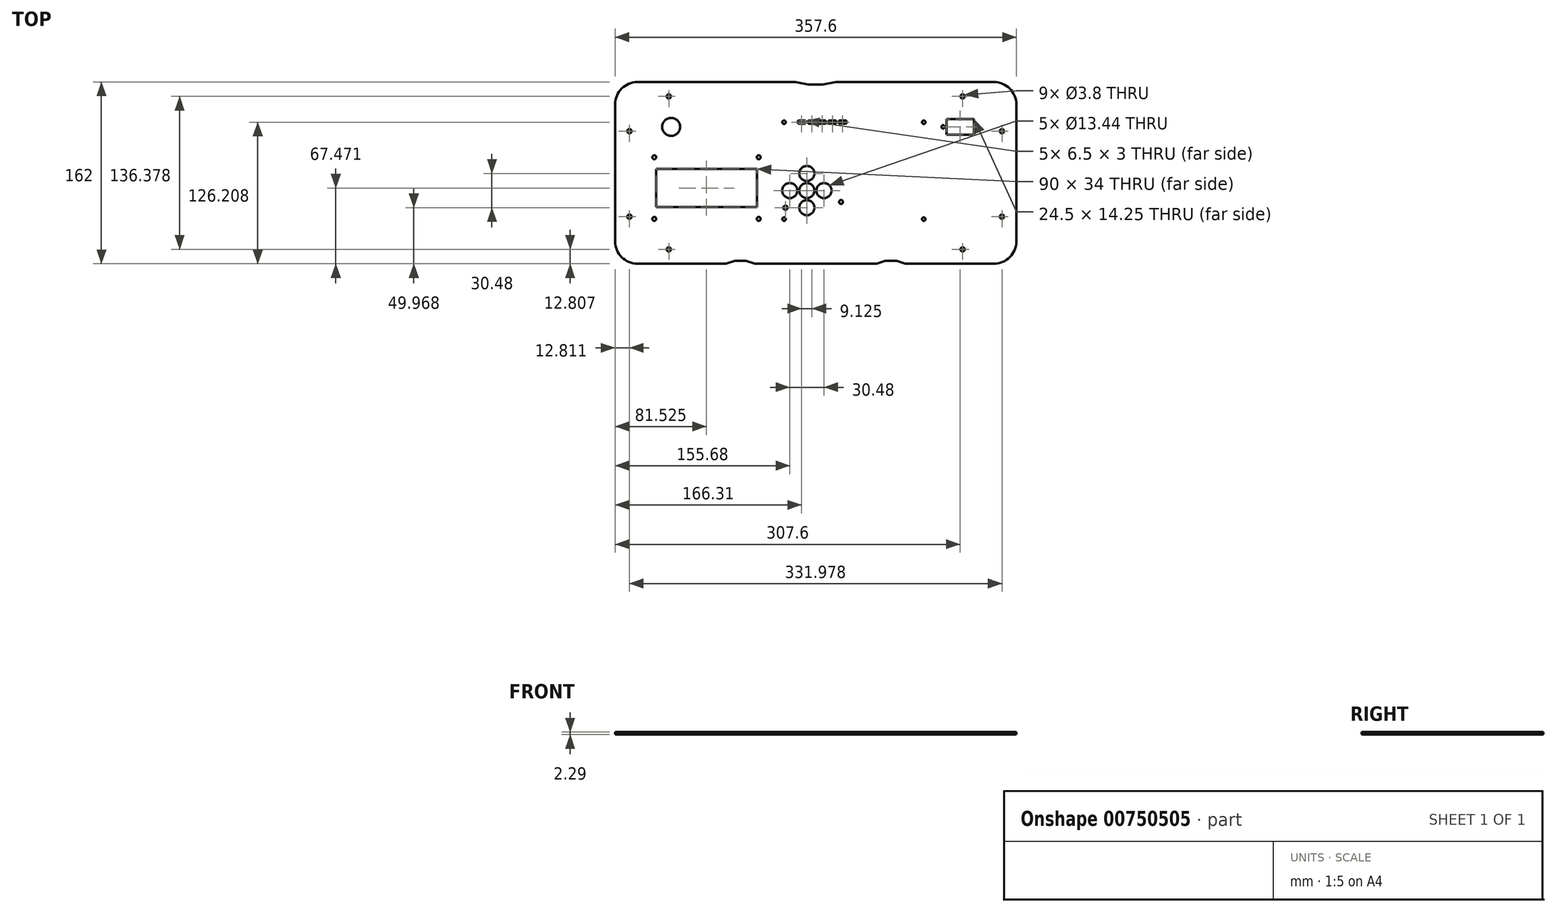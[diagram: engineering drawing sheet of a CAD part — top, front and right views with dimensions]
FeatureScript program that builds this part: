
annotation { "Feature Type Name" : "Feature", "Feature Type Description" : "" }
export const myFeature = defineFeature(function(context is Context, id is Id, definition is map)
    precondition{}
    {
        {
            var Q0;
            Q0=qCreatedBy(makeId("Top.planeOp"),FACE);
            var sketch = newSketch(context, id + "F0", { "sketchPlane" : qUnion([Q0])});
            skLineSegment(sketch, "E0.bottom", {"start": v(-158.73, 79.95) * mm, "end": v(-17.96, 79.95) * mm});
            skLineSegment(sketch, "E0.top", {"start": v(-158.73, -82.05) * mm, "end": v(-79.8, -82.05) * mm});
            skLineSegment(sketch, "E0.left", {"start": v(-178.8, 59.88) * mm, "end": v(-178.8, -61.99) * mm});
            skLineSegment(sketch, "E0.right", {"start": v(178.8, 59.88) * mm, "end": v(178.8, -61.99) * mm});
            skPoint(sketch, "E1.visualSharp", {"position": v(-178.8, 79.95) * mm});
            skArc(sketch, "E1.filletArc", {"start": v(-158.73, 79.95) * mm, "mid": v(-172.92, 74.07) * mm, "end": v(-178.8, 59.88) * mm});
            skPoint(sketch, "E2.visualSharp", {"position": v(-178.8, -82.05) * mm});
            skArc(sketch, "E2.filletArc", {"start": v(-178.8, -61.99) * mm, "mid": v(-172.92, -76.18) * mm, "end": v(-158.73, -82.05) * mm});
            skPoint(sketch, "E3.visualSharp", {"position": v(178.8, -82.05) * mm});
            skArc(sketch, "E3.filletArc", {"start": v(158.73, -82.05) * mm, "mid": v(172.92, -76.18) * mm, "end": v(178.8, -61.99) * mm});
            skPoint(sketch, "E4.visualSharp", {"position": v(178.8, 79.95) * mm});
            skArc(sketch, "E4.filletArc", {"start": v(178.8, 59.88) * mm, "mid": v(172.92, 74.07) * mm, "end": v(158.73, 79.95) * mm});
            skCircle(sketch, "E5", {"center": v(-130.9, 67.13) * mm, "radius": 1.9 * mm});
            skCircle(sketch, "E6", {"center": v(-165.99, 36.1) * mm, "radius": 1.9 * mm});
            skCircle(sketch, "E7", {"center": v(-165.99, -40.1) * mm, "radius": 1.9 * mm});
            skCircle(sketch, "E8", {"center": v(-130.9, -69.24) * mm, "radius": 1.9 * mm});
            skCircle(sketch, "E9.MirrorC", {"center": v(165.99, 36.1) * mm, "radius": 1.9 * mm});
            skCircle(sketch, "E10.MirrorC", {"center": v(130.9, 67.13) * mm, "radius": 1.9 * mm});
            skCircle(sketch, "E11.MirrorC", {"center": v(165.99, -40.1) * mm, "radius": 1.9 * mm});
            skCircle(sketch, "E12.MirrorC", {"center": v(130.9, -69.24) * mm, "radius": 1.9 * mm});
            skArc(sketch, "E13.0", {"start": v(-158.73, 60.9) * mm, "mid": v(-159.45, 60.6) * mm, "end": v(-159.75, 59.88) * mm});
            skLineSegment(sketch, "E13.1", {"start": v(-159.75, 59.88) * mm, "end": v(-159.75, -61.99) * mm, "construction": true});
            skLineSegment(sketch, "E13.2", {"start": v(-158.73, 60.9) * mm, "end": v(158.73, 60.9) * mm, "construction": true});
            skArc(sketch, "E13.3", {"start": v(-159.75, -61.99) * mm, "mid": v(-159.45, -62.7) * mm, "end": v(-158.73, -63) * mm});
            skArc(sketch, "E13.4", {"start": v(159.75, 59.88) * mm, "mid": v(159.45, 60.6) * mm, "end": v(158.73, 60.9) * mm});
            skLineSegment(sketch, "E13.5", {"start": v(159.75, 59.88) * mm, "end": v(159.75, -61.99) * mm, "construction": true});
            skArc(sketch, "E13.6", {"start": v(158.73, -63) * mm, "mid": v(159.45, -62.7) * mm, "end": v(159.75, -61.99) * mm});
            skLineSegment(sketch, "E13.7", {"start": v(-158.73, -63) * mm, "end": v(158.73, -63) * mm, "construction": true});
            skLineSegment(sketch, "E14", {"start": v(0, 79.95) * mm, "end": v(0, 0) * mm, "construction": true});
            skLineSegment(sketch, "E15", {"start": v(178.8, 0) * mm, "end": v(0, 0) * mm, "construction": true});
            skCircle(sketch, "E16", {"center": v(-128.8, 39.95) * mm, "radius": 8.05 * mm});
            skCircle(sketch, "E17", {"center": v(113.53, 39.95) * mm, "radius": 1.48 * mm});
            skLineSegment(sketch, "E18.bottom", {"start": v(116.55, 47.07) * mm, "end": v(141.05, 47.07) * mm});
            skLineSegment(sketch, "E18.top", {"start": v(116.55, 32.82) * mm, "end": v(141.05, 32.82) * mm});
            skLineSegment(sketch, "E18.left", {"start": v(116.55, 47.07) * mm, "end": v(116.55, 32.82) * mm});
            skLineSegment(sketch, "E18.right", {"start": v(141.05, 47.07) * mm, "end": v(141.05, 32.82) * mm});
            skLineSegment(sketch, "E19", {"start": v(141.05, 39.95) * mm, "end": v(116.55, 39.95) * mm, "construction": true});
            skCircle(sketch, "E20", {"center": v(144.08, 39.96) * mm, "radius": 1.48 * mm});
            skLineSegment(sketch, "E21", {"start": v(128.8, 47.07) * mm, "end": v(128.8, 32.82) * mm, "construction": true});
            skLineSegment(sketch, "E22", {"start": v(-6.5, 77.6) * mm, "end": v(6.5, 77.6) * mm});
            skLineSegment(sketch, "E23", {"start": v(0, 77.6) * mm, "end": v(0, 79.95) * mm, "construction": true});
            skLineSegment(sketch, "E24", {"start": v(6.5, 77.6) * mm, "end": v(17.96, 79.95) * mm});
            skLineSegment(sketch, "E25", {"start": v(-6.5, 77.6) * mm, "end": v(-17.96, 79.95) * mm});
            skLineSegment(sketch, "E26", {"start": v(17.96, 79.95) * mm, "end": v(158.73, 79.95) * mm});
            skPoint(sketch, "E27", {"position": v(-79.8, -82.05) * mm});
            skPoint(sketch, "E28", {"position": v(-54.3, -82.05) * mm});
            skLineSegment(sketch, "E29", {"start": v(-72.08, -79.45) * mm, "end": v(-62.08, -79.45) * mm});
            skLineSegment(sketch, "E30", {"start": v(-79.8, -82.05) * mm, "end": v(-72.08, -79.45) * mm});
            skLineSegment(sketch, "E31", {"start": v(-62.08, -79.45) * mm, "end": v(-54.3, -82.05) * mm});
            skLineSegment(sketch, "E32.trimOffspring", {"start": v(-54.3, -82.05) * mm, "end": v(54.3, -82.05) * mm});
            skPoint(sketch, "E33", {"position": v(79.8, -82.05) * mm});
            skPoint(sketch, "E34", {"position": v(54.3, -82.05) * mm});
            skLineSegment(sketch, "E35", {"start": v(62.08, -79.45) * mm, "end": v(72.08, -79.45) * mm});
            skLineSegment(sketch, "E36", {"start": v(79.8, -82.05) * mm, "end": v(72.08, -79.45) * mm});
            skLineSegment(sketch, "E37", {"start": v(54.3, -82.05) * mm, "end": v(62.08, -79.45) * mm});
            skLineSegment(sketch, "E38.trimOffspring", {"start": v(79.8, -82.05) * mm, "end": v(158.73, -82.05) * mm});
            skSolve(sketch);
        }
        {
            var Q0;
            Q0=makeQuery(id+"F0.imprint","IMPRINT",FACE,{"disambiguationData":[TD([[makeQuery(id+"F0.imprint","IMPRINT",EDGE,{"derivedFrom":sQuery(id+"F0.wireOp",EDGE,"E0.bottom")}),-1.0]])]});
            var sketch = newSketch(context, id + "F1", { "sketchPlane" : qUnion([Q0])});
            skLineSegment(sketch, "E39", {"start": v(98.8, -42.24) * mm, "end": v(98.8, -28.27) * mm, "construction": true});
            skLineSegment(sketch, "E40", {"start": v(98.8, -22.69) * mm, "end": v(98.8, 44.12) * mm, "construction": true});
            skLineSegment(sketch, "E41", {"start": v(-30.74, 44.12) * mm, "end": v(-30.74, -42.24) * mm, "construction": true});
            skArc(sketch, "E42", {"start": v(98.8, 44.12) * mm, "mid": v(98.06, 45.91) * mm, "end": v(96.26, 46.66) * mm, "construction": true});
            skArc(sketch, "E43", {"start": v(96.26, -44.78) * mm, "mid": v(98.06, -44.04) * mm, "end": v(98.8, -42.24) * mm, "construction": true});
            skArc(sketch, "E44", {"start": v(-30.74, -42.24) * mm, "mid": v(-30, -44.04) * mm, "end": v(-28.2, -44.78) * mm, "construction": true});
            skArc(sketch, "E45", {"start": v(-28.2, 46.66) * mm, "mid": v(-30, 45.91) * mm, "end": v(-30.74, 44.12) * mm, "construction": true});
            skLineSegment(sketch, "E46", {"start": v(-28.2, -44.78) * mm, "end": v(96.26, -44.78) * mm, "construction": true});
            skArc(sketch, "E47", {"start": v(98.3, -23.2) * mm, "mid": v(98.65, -23.05) * mm, "end": v(98.8, -22.69) * mm, "construction": true});
            skArc(sketch, "E48", {"start": v(98.8, -28.27) * mm, "mid": v(98.65, -27.91) * mm, "end": v(98.3, -27.76) * mm, "construction": true});
            skArc(sketch, "E49", {"start": v(97.43, -27.26) * mm, "mid": v(97.65, -27.87) * mm, "end": v(98.3, -27.76) * mm, "construction": true});
            skArc(sketch, "E50", {"start": v(98.3, -23.2) * mm, "mid": v(97.93, -23.34) * mm, "end": v(97.78, -23.7) * mm, "construction": true});
            skLineSegment(sketch, "E51", {"start": v(97.78, -27.26) * mm, "end": v(97.78, -23.7) * mm, "construction": true});
            skCircle(sketch, "E52", {"center": v(96.28, -42.24) * mm, "radius": 1.55 * mm});
            skCircle(sketch, "E53", {"center": v(96.28, 44.12) * mm, "radius": 1.55 * mm});
            skCircle(sketch, "E54", {"center": v(-28.2, 44.12) * mm, "radius": 1.55 * mm});
            skCircle(sketch, "E55", {"center": v(-28.2, -42.24) * mm, "radius": 1.55 * mm});
            skCircle(sketch, "E56", {"center": v(-18.62, -16.84) * mm, "radius": 0.93 * mm, "construction": true});
            skCircle(sketch, "E57", {"center": v(-27.62, -16.84) * mm, "radius": 0.93 * mm, "construction": true});
            skCircle(sketch, "E58", {"center": v(11.86, -16.84) * mm, "radius": 0.93 * mm, "construction": true});
            skCircle(sketch, "E59", {"center": v(2.86, -16.84) * mm, "radius": 0.93 * mm, "construction": true});
            skCircle(sketch, "E60", {"center": v(-7.88, -36.58) * mm, "radius": 0.93 * mm, "construction": true});
            skCircle(sketch, "E61", {"center": v(-7.88, -27.58) * mm, "radius": 0.93 * mm, "construction": true});
            skCircle(sketch, "E62", {"center": v(-7.88, -6.1) * mm, "radius": 0.93 * mm, "construction": true});
            skCircle(sketch, "E63", {"center": v(-7.88, 2.9) * mm, "radius": 0.93 * mm, "construction": true});
            skCircle(sketch, "E64", {"center": v(-3.38, -16.84) * mm, "radius": 0.93 * mm, "construction": true});
            skCircle(sketch, "E65", {"center": v(-12.38, -16.84) * mm, "radius": 0.93 * mm, "construction": true});
            skCircle(sketch, "E66", {"center": v(-26.94, -32.08) * mm, "radius": 1.9 * mm});
            skCircle(sketch, "E67", {"center": v(22.6, -27) * mm, "radius": 1.75 * mm});
            skLineSegment(sketch, "E68", {"start": v(-27.62, -16.84) * mm, "end": v(-18.62, -16.84) * mm, "construction": true});
            skLineSegment(sketch, "E69", {"start": v(-12.38, -16.84) * mm, "end": v(-3.38, -16.84) * mm, "construction": true});
            skLineSegment(sketch, "E70", {"start": v(2.86, -16.84) * mm, "end": v(11.86, -16.84) * mm, "construction": true});
            skLineSegment(sketch, "E71", {"start": v(-7.88, -27.58) * mm, "end": v(-7.88, -36.58) * mm, "construction": true});
            skLineSegment(sketch, "E72", {"start": v(-7.88, 2.9) * mm, "end": v(-7.88, -6.1) * mm, "construction": true});
            skCircle(sketch, "E73", {"center": v(-23.12, -16.84) * mm, "radius": 6.72 * mm});
            skCircle(sketch, "E74", {"center": v(-7.88, -16.84) * mm, "radius": 6.72 * mm});
            skCircle(sketch, "E75", {"center": v(-7.88, -1.6) * mm, "radius": 6.72 * mm});
            skCircle(sketch, "E76", {"center": v(7.36, -16.84) * mm, "radius": 6.72 * mm});
            skCircle(sketch, "E77", {"center": v(-7.88, -32.08) * mm, "radius": 6.72 * mm});
            skLineSegment(sketch, "E78.bottom", {"start": v(-15.74, 45.66) * mm, "end": v(-9.24, 45.66) * mm});
            skLineSegment(sketch, "E78.top", {"start": v(-15.74, 42.66) * mm, "end": v(-9.24, 42.66) * mm});
            skLineSegment(sketch, "E78.left", {"start": v(-15.74, 45.66) * mm, "end": v(-15.74, 42.66) * mm});
            skLineSegment(sketch, "E78.right", {"start": v(-9.24, 45.66) * mm, "end": v(-9.24, 42.66) * mm});
            skLineSegment(sketch, "E79.bottom", {"start": v(-6.61, 45.66) * mm, "end": v(-0.11, 45.66) * mm});
            skLineSegment(sketch, "E79.top", {"start": v(-6.61, 42.66) * mm, "end": v(-0.11, 42.66) * mm});
            skLineSegment(sketch, "E79.left", {"start": v(-6.61, 45.66) * mm, "end": v(-6.61, 42.66) * mm});
            skLineSegment(sketch, "E79.right", {"start": v(-0.11, 45.66) * mm, "end": v(-0.11, 42.66) * mm});
            skLineSegment(sketch, "E80.bottom", {"start": v(2.51, 45.66) * mm, "end": v(9.01, 45.66) * mm});
            skLineSegment(sketch, "E80.top", {"start": v(2.51, 42.66) * mm, "end": v(9.01, 42.66) * mm});
            skLineSegment(sketch, "E80.left", {"start": v(2.51, 45.66) * mm, "end": v(2.51, 42.66) * mm});
            skLineSegment(sketch, "E80.right", {"start": v(9.01, 45.66) * mm, "end": v(9.01, 42.66) * mm});
            skLineSegment(sketch, "E81.bottom", {"start": v(11.64, 45.66) * mm, "end": v(18.14, 45.66) * mm});
            skLineSegment(sketch, "E81.top", {"start": v(11.64, 42.66) * mm, "end": v(18.14, 42.66) * mm});
            skLineSegment(sketch, "E81.left", {"start": v(11.64, 45.66) * mm, "end": v(11.64, 42.66) * mm});
            skLineSegment(sketch, "E81.right", {"start": v(18.14, 45.66) * mm, "end": v(18.14, 42.66) * mm});
            skLineSegment(sketch, "E82.bottom", {"start": v(20.76, 45.66) * mm, "end": v(27.26, 45.66) * mm});
            skLineSegment(sketch, "E82.top", {"start": v(20.76, 42.66) * mm, "end": v(27.26, 42.66) * mm});
            skLineSegment(sketch, "E82.left", {"start": v(20.76, 45.66) * mm, "end": v(20.76, 42.66) * mm});
            skLineSegment(sketch, "E82.right", {"start": v(27.26, 45.66) * mm, "end": v(27.26, 42.66) * mm});
            skLineSegment(sketch, "E83", {"start": v(-28.2, 46.66) * mm, "end": v(96.26, 46.66) * mm, "construction": true});
            skSolve(sketch);
        }
        {
            var Q0;
            Q0=makeQuery(id+"F0.imprint","IMPRINT",FACE,{"disambiguationData":[TD([[makeQuery(id+"F0.imprint","IMPRINT",EDGE,{"derivedFrom":sQuery(id+"F0.wireOp",EDGE,"E0.bottom")}),-1.0]])]});
            var sketch = newSketch(context, id + "F2", { "sketchPlane" : qUnion([Q0])});
            skLineSegment(sketch, "E84", {"start": v(-146.3, 15.45) * mm, "end": v(-48.25, 15.45) * mm, "construction": true});
            skLineSegment(sketch, "E85", {"start": v(-146.3, -44.6) * mm, "end": v(-48.25, -44.6) * mm, "construction": true});
            skLineSegment(sketch, "E86", {"start": v(-146.3, 15.45) * mm, "end": v(-146.3, -44.6) * mm, "construction": true});
            skLineSegment(sketch, "E87", {"start": v(-48.25, 15.45) * mm, "end": v(-48.25, -44.6) * mm, "construction": true});
            skLineSegment(sketch, "E88", {"start": v(-145.8, 5.2) * mm, "end": v(-48.75, 5.2) * mm, "construction": true});
            skLineSegment(sketch, "E89", {"start": v(-145.8, -34.5) * mm, "end": v(-48.75, -34.5) * mm, "construction": true});
            skLineSegment(sketch, "E90", {"start": v(-145.8, 5.2) * mm, "end": v(-145.8, -34.5) * mm, "construction": true});
            skLineSegment(sketch, "E91", {"start": v(-48.75, 5.2) * mm, "end": v(-48.75, -34.5) * mm, "construction": true});
            skCircle(sketch, "E92", {"center": v(-143.8, 12.9) * mm, "radius": 1.75 * mm});
            skCircle(sketch, "E93", {"center": v(-143.8, -42.05) * mm, "radius": 1.75 * mm});
            skCircle(sketch, "E94", {"center": v(-50.75, 12.9) * mm, "radius": 1.75 * mm});
            skCircle(sketch, "E95", {"center": v(-50.75, -42.05) * mm, "radius": 1.75 * mm});
            skLineSegment(sketch, "E96", {"start": v(-135.2, -1.55) * mm, "end": v(-59.2, -1.55) * mm, "construction": true});
            skLineSegment(sketch, "E97", {"start": v(-135.2, -27.8) * mm, "end": v(-59.2, -27.8) * mm, "construction": true});
            skLineSegment(sketch, "E98", {"start": v(-135.2, -1.55) * mm, "end": v(-135.2, -27.8) * mm, "construction": true});
            skLineSegment(sketch, "E99", {"start": v(-59.2, -1.55) * mm, "end": v(-59.2, -27.8) * mm, "construction": true});
            skLineSegment(sketch, "E100", {"start": v(-142.28, 2.42) * mm, "end": v(-52.28, 2.42) * mm});
            skLineSegment(sketch, "E101", {"start": v(-142.28, -31.58) * mm, "end": v(-52.28, -31.58) * mm});
            skLineSegment(sketch, "E102", {"start": v(-142.28, 2.42) * mm, "end": v(-142.28, -31.58) * mm});
            skLineSegment(sketch, "E103", {"start": v(-52.28, 2.42) * mm, "end": v(-52.28, -31.58) * mm});
            skSolve(sketch);
        }
        {
            var Q0;
            Q0 = qSketchRegion(id + "F0", true);
            extrude(context, id + "F3", {"entities" : qUnion([Q0]), "depth" : 2.3 * mm, "offsetDistance" : 25 * mm});
        }
        {
            var Q0;
            Q0 = qSketchRegion(id + "F2", true);
            extrude(context, id + "F4", {"entities" : qUnion([Q0]), "operationType" : NewBodyOperationType.REMOVE, "oppositeDirection" : true, "depth" : -2.3 * mm, "offsetDistance" : 25 * mm});
        }
        {
            var Q0;
            Q0 = qSketchRegion(id + "F1", true);
            extrude(context, id + "F5", {"entities" : qUnion([Q0]), "operationType" : NewBodyOperationType.REMOVE, "oppositeDirection" : true, "depth" : -2.3 * mm, "offsetDistance" : 25 * mm});
        }
    });
